FCSTD DOCUMENT  (FreeCAD 0.20R0.20)
Label: 004
License: All rights reserved
LicenseURL: http://en.wikipedia.org/wiki/All_rights_reserved
objects: Sketcher::SketchObject×1
note: 1 computed .brp shape members not serialized (recipe doc carries the construction recipe); baked Part::Feature solids carry a one-line shape summary decoded from their .brp

FEATURE [Sketcher::SketchObject] Sketch
  FullyConstrained = true
  sketch-geometry (25):
    g0: LineSegment StartX=80 StartY=80 StartZ=0 EndX=74 EndY=80 EndZ=0
    g1: LineSegment StartX=80 StartY=80 StartZ=0 EndX=80 EndY=74 EndZ=0
    g2: LineSegment StartX=0 StartY=80 StartZ=0 EndX=6 EndY=80 EndZ=0
    g3: LineSegment StartX=80 StartY=0 StartZ=0 EndX=80 EndY=6 EndZ=0
    g4: LineSegment StartX=0 StartY=0 StartZ=0 EndX=0 EndY=6 EndZ=0
    g5: LineSegment StartX=0 StartY=0 StartZ=0 EndX=6 EndY=0 EndZ=0
    g6: LineSegment StartX=80 StartY=0 StartZ=0 EndX=74 EndY=0 EndZ=0
    g7: LineSegment StartX=0 StartY=80 StartZ=0 EndX=0 EndY=74 EndZ=0
    g8: LineSegment StartX=70 StartY=74 StartZ=0 EndX=40 EndY=44 EndZ=0
    g9: LineSegment StartX=10 StartY=6 StartZ=0 EndX=40 EndY=36 EndZ=0
    g10: LineSegment StartX=10 StartY=74 StartZ=0 EndX=40 EndY=44 EndZ=0
    g11: LineSegment StartX=6 StartY=70 StartZ=0 EndX=36 EndY=40 EndZ=0
    g12: LineSegment StartX=40 StartY=36 StartZ=0 EndX=70 EndY=6 EndZ=0
    g13: LineSegment StartX=44 StartY=40 StartZ=0 EndX=74 EndY=10 EndZ=0
    g14: LineSegment StartX=36 StartY=40 StartZ=0 EndX=6 EndY=10 EndZ=0
    g15: LineSegment StartX=44 StartY=40 StartZ=0 EndX=74 EndY=70 EndZ=0
    g16: LineSegment StartX=70 StartY=74 StartZ=0 EndX=10 EndY=74 EndZ=0
    g17: LineSegment StartX=74 StartY=10 StartZ=0 EndX=74 EndY=70 EndZ=0
    g18: LineSegment StartX=10 StartY=6 StartZ=0 EndX=70 EndY=6 EndZ=0
    g19: LineSegment StartX=6 StartY=70 StartZ=0 EndX=6 EndY=10 EndZ=0
    g20: LineSegment StartX=6 StartY=80 StartZ=0 EndX=74 EndY=80 EndZ=0
    g21: LineSegment StartX=80 StartY=74 StartZ=0 EndX=80 EndY=6 EndZ=0
    g22: LineSegment StartX=74 StartY=0 StartZ=0 EndX=6 EndY=0 EndZ=0
    g23: LineSegment StartX=0 StartY=6 StartZ=0 EndX=0 EndY=74 EndZ=0
    g24: LineSegment StartX=36 StartY=40 StartZ=0 EndX=40 EndY=40 EndZ=0
  constraints (63):
    c: Horizontal(g0)
    c: Distance(g0) = 6
    c: Block(g0)
    c: Coincident(g1,g0)
    c: Vertical(g1)
    c: Horizontal(g2)
    c: Vertical(g3)
    c: Distance(g1) = 6
    c: Distance(g2) = 6
    c: Distance(g3) = 6
    c: Block(g2)
    c: Block(g3)
    c: Coincident(g4,g-1)
    c: Vertical(g4)
    c: Coincident(g5,g4)
    c: Horizontal(g5)
    c: Coincident(g6,g3)
    c: Horizontal(g6)
    c: Coincident(g7,g2)
    c: Vertical(g7)
    c: Distance(g7) = 6
    c: Distance(g4) = 6
    c: Distance(g5) = 6
    c: Distance(g6) = 6
    c: Coincident(g8,g10)
    c: Coincident(g14,g11)
    c: Coincident(g9,g12)
    c: Coincident(g15,g13)
    c: Block(g15)
    c: Block(g8)
    c: Block(g14)
    c: Block(g12)
    c: Block(g13)
    c: Block(g9)
    c: Block(g11)
    c: Block(g10)
    c: Block(g16)
    c: Block(g17)
    c: Block(g18)
    c: Block(g19)
    c: Coincident(g8,g16)
    c: Coincident(g15,g17)
    c: Coincident(g13,g17)
    c: Coincident(g12,g18)
    c: Coincident(g9,g18)
    c: Coincident(g14,g19)
    c: Coincident(g11,g19)
    c: Coincident(g10,g16)
    c: Coincident(g20,g2)
    c: Coincident(g20,g0)
    c: Horizontal(g20)
    c: Coincident(g21,g1)
    c: Coincident(g21,g3)
    c: Vertical(g21)
    c: Coincident(g22,g6)
    c: Coincident(g22,g5)
    c: Horizontal(g22)
    c: Coincident(g23,g4)
    c: Coincident(g23,g7)
    c: Vertical(g23)
    c: Coincident(g24,g11)
    c: Horizontal(g24)
    c: Distance(g24) = 4
